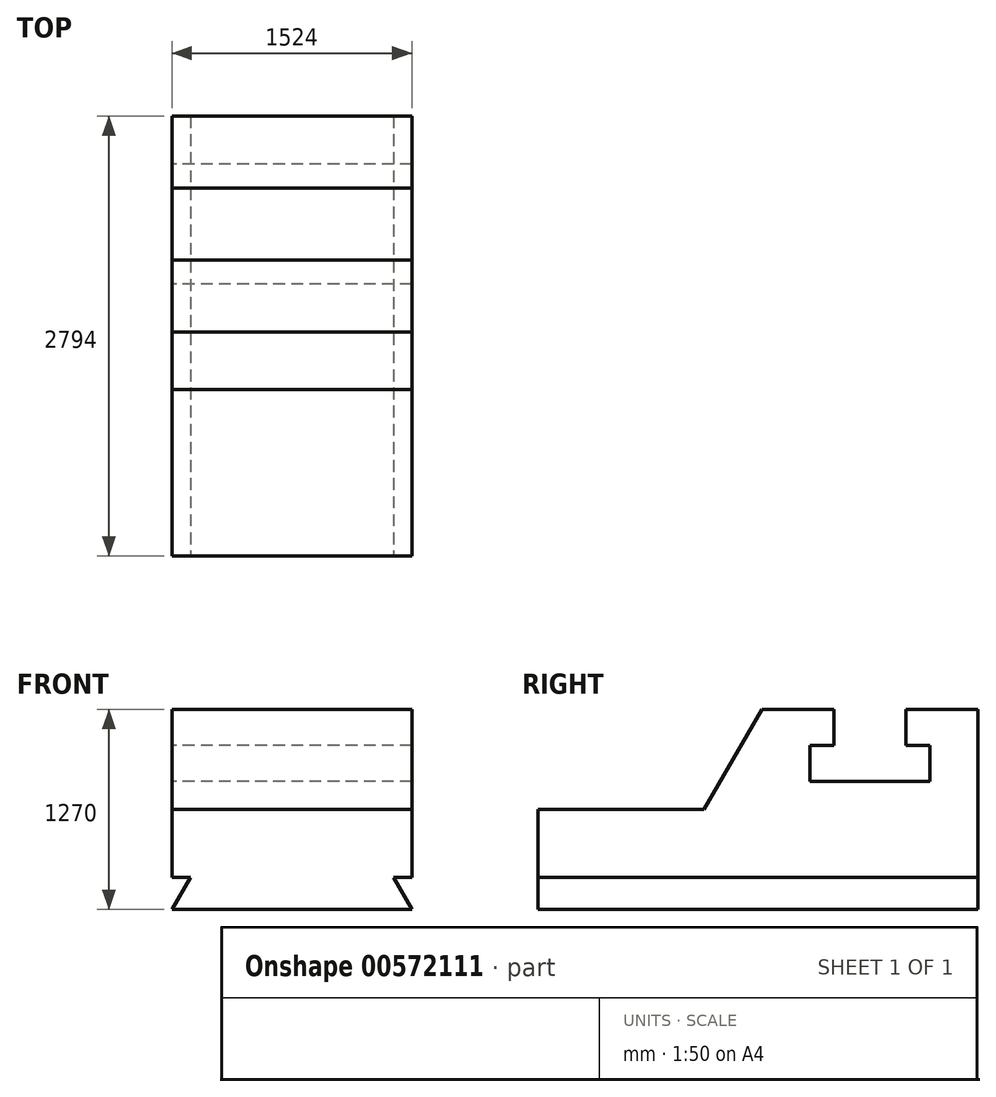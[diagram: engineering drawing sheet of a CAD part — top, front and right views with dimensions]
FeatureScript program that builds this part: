
annotation { "Feature Type Name" : "Feature", "Feature Type Description" : "" }
export const myFeature = defineFeature(function(context is Context, id is Id, definition is map)
    precondition{}
    {
        {
            var Q0;
            Q0=qCreatedBy(makeId("Right.planeOp"),FACE);
            var sketch = newSketch(context, id + "F0", { "sketchPlane" : qUnion([Q0])});
            skLineSegment(sketch, "E0", {"start": v(0, 0) * mm, "end": v(0, -1270) * mm});
            skLineSegment(sketch, "E1", {"start": v(0, -1270) * mm, "end": v(-2794, -1270) * mm});
            skLineSegment(sketch, "E2", {"start": v(-2794, -1270) * mm, "end": v(-2794, -635) * mm});
            skLineSegment(sketch, "E3", {"start": v(-2794, -635) * mm, "end": v(-1738.22, -635) * mm});
            skLineSegment(sketch, "E4", {"start": v(0, 0) * mm, "end": v(-457.2, 0) * mm});
            skLineSegment(sketch, "E5", {"start": v(-457.2, 0) * mm, "end": v(-914.4, 0) * mm});
            skLineSegment(sketch, "E6", {"start": v(-914.4, 0) * mm, "end": v(-1371.6, 0) * mm});
            skLineSegment(sketch, "E7", {"start": v(-1371.6, 0) * mm, "end": v(-1738.22, -635) * mm});
            skLineSegment(sketch, "E8", {"start": v(-457.2, 0) * mm, "end": v(-457.2, -228.6) * mm});
            skLineSegment(sketch, "E9", {"start": v(-457.2, -228.6) * mm, "end": v(-304.8, -228.6) * mm});
            skLineSegment(sketch, "E10", {"start": v(-304.8, -228.6) * mm, "end": v(-304.8, -457.2) * mm});
            skLineSegment(sketch, "E11", {"start": v(-304.8, -457.2) * mm, "end": v(-1066.8, -457.2) * mm});
            skLineSegment(sketch, "E12", {"start": v(-1066.8, -457.2) * mm, "end": v(-1066.8, -228.6) * mm});
            skLineSegment(sketch, "E13", {"start": v(-1066.8, -228.6) * mm, "end": v(-914.4, -228.6) * mm});
            skLineSegment(sketch, "E14", {"start": v(-914.4, -228.6) * mm, "end": v(-914.4, 0) * mm});
            skSolve(sketch);
        }
        {
            var Q0;
            Q0=makeQuery(id+"F0.imprint","IMPRINT",FACE,{"disambiguationData":[TD([[makeQuery(id+"F0.imprint","IMPRINT",EDGE,{"derivedFrom":sQuery(id+"F0.wireOp",EDGE,"E0")}),-1.0]])]});
            extrude(context, id + "F1", {"entities" : qUnion([Q0]), "depth" : 1524 * mm, "offsetDistance" : 25.4 * mm});
        }
        {
            var Q0;
            Q0=makeQuery(id+"F1.opExtrude","SWEPT_FACE",FACE,{"disambiguationData":[OSD([sQuery(id+"F0.wireOp",EDGE,"E2")])]});
            var sketch = newSketch(context, id + "F2", { "sketchPlane" : qUnion([Q0])});
            skLineSegment(sketch, "E15", {"start": v(0, -1270) * mm, "end": v(0, -1066.8) * mm});
            skLineSegment(sketch, "E16", {"start": v(0, -1066.8) * mm, "end": v(117.32, -1066.8) * mm});
            skLineSegment(sketch, "E17", {"start": v(0, -1270) * mm, "end": v(117.32, -1066.8) * mm});
            skLineSegment(sketch, "E18", {"start": v(1524, -1270) * mm, "end": v(1524, -1066.8) * mm});
            skLineSegment(sketch, "E19", {"start": v(1524, -1066.8) * mm, "end": v(1406.68, -1066.8) * mm});
            skLineSegment(sketch, "E20", {"start": v(1524, -1270) * mm, "end": v(1406.68, -1066.8) * mm});
            skSolve(sketch);
        }
        {
            var Q0;
            Q0=makeQuery(id+"F2.imprint","IMPRINT",FACE,{"disambiguationData":[TD([[makeQuery(id+"F2.imprint","IMPRINT",EDGE,{"derivedFrom":sQuery(id+"F2.wireOp",EDGE,"E15")}),-1.0]])]});
            var Q1;
            Q1=makeQuery(id+"F2.imprint","IMPRINT",FACE,{"disambiguationData":[TD([[makeQuery(id+"F2.imprint","IMPRINT",EDGE,{"derivedFrom":sQuery(id+"F2.wireOp",EDGE,"E18")}),1.0]])]});
            extrude(context, id + "F3", {"entities" : qUnion([Q0, Q1]), "operationType" : NewBodyOperationType.REMOVE, "endBound" : BoundingType.THROUGH_ALL, "oppositeDirection" : true, "depth" : 25.4 * mm, "offsetDistance" : 25.4 * mm});
        }
    });
